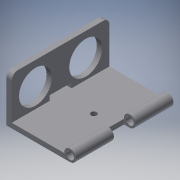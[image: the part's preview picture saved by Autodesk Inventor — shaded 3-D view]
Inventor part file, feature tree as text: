
AUTODESK INVENTOR PART (.ipt)
format: ipt  version: 2016 (Build 200138000, 138)  size: 327,168 bytes
history: native  units: in
note: dims shown in document units (in); Inventor stores cm internally (conversion verified against a paired STEP export)
features: extrude x20, sketch x20, projected_geometry x6, reference x3, fillet x2, plane x1
ambient origin geometry x8: Origin, YZ Plane, XZ Plane, XY Plane, X Axis, Y Axis, Z Axis, Center Point
bodies: Solid1 (feature_tree)
feature tree (52):
  extrude  "Extrusion1"  Depth=0.05in
  plane  "Work Plane1"
  extrude  "Extrusion2"  Depth=0.1496in
  extrude  "Extrusion3"  [1 undecoded]
  sketch  "Sketch4"  dims[d7=0.4in d8=0.0in d9=1.1in]
  extrude  "Extrusion4"  Depth=1.1in
  extrude  "Extrusion5"  Depth=1.1in
  extrude  "Extrusion6"  Depth=1.05in
  extrude  "Extrusion7"  Depth=1.05in
  extrude  "Extrusion8"  Depth=1.2in
  extrude  "Extrusion9"  Depth=1.2in
  extrude  "Extrusion10"  Depth=1.1in
  fillet  "Fillet1"  Radius=1.1in
  extrude  "Extrusion12"  Depth=1.0in TaperAngle=0.0deg
  extrude  "Extrusion13"  Depth=0.05in TaperAngle=0.0deg
  extrude  "Extrusion14"  Depth=0.8661in TaperAngle=0.0deg
  extrude  "Extrusion15"  Depth=0.3937in TaperAngle=0.0deg
  extrude  "Extrusion16"  Depth=0.125in TaperAngle=0.0deg
  extrude  "Extrusion17"  Depth=0.5906in TaperAngle=0.0deg
  extrude  "Extrusion18"  Depth=0.6693in
  extrude  "Extrusion19"  Depth=1.0in TaperAngle=0.0deg
  extrude  "Extrusion20"  Depth=0.0197in TaperAngle=0.0deg
  fillet  "Fillet2"  Radius=0.08in
  extrude  "Extrusion21"  Depth=0.44in
  sketch  "Sketch1"  dims[d0=0.15in d1=0.05in]
  sketch  "Sketch2"  dims[d2=0.2362in d3=0.1496in]
  sketch  "Sketch3"  dims[d4=1.2in d5=0.0in d6=-0.4in]
  sketch  "Sketch5"  dims[d10=1.1in d11=1.1in]
  sketch  "Sketch6"  dims[d12=0.05in d13=1.05in]
  sketch  "Sketch7"  dims[d14=0.05in d15=1.05in]
  sketch  "Sketch8"  dims[d16=1.0in d17=0.0in d18=1.2in]
  reference  "Reference1"
  sketch  "Sketch9"  dims[d19=1.2in d20=1.2in]
  projected_geometry  "Projected Loop1"
  sketch  "Sketch10"  dims[d21=1.1in d22=1.1in d23=1.1in]
  projected_geometry  "Projected Loop2"
  sketch  "Sketch12"  dims[d24=1.0in d25=0.0in d26=1.0in d27=0.0in]
  projected_geometry  "Projected Loop3"
  sketch  "Sketch13"  dims[d28=0.05in d29=0.0in d30=0.05in d31=0.0in]
  sketch  "Sketch14"  dims[d32=0.1083in d35=0.8661in d36=0.0in]
  projected_geometry  "Projected Loop4"
  sketch  "Sketch15"  dims[d37=0.3937in d38=0.0in d39=0.3937in d40=0.0in]
  sketch  "Sketch16"  dims[d45=0.125in d46=0.4724in d47=0.0in]
  reference  "Reference4"
  reference  "Reference5"
  sketch  "Sketch17"  dims[d48=199.0in d49=0.0in d50=0.5906in d51=0.0in]
  projected_geometry  "Projected Loop5"
  sketch  "Sketch18"  dims[d52=0.5906in d53=0.0in d54=0.6693in]
  projected_geometry  "Projected Loop6"
  sketch  "Sketch19"  dims[d55=0.6693in d56=1.0in d57=0.0in]
  sketch  "Sketch20"  dims[d58=0.0197in d59=0.0in d60=0.0197in d61=0.0in d62=0.08in d63=0.0in]
  sketch  "Sketch21"  dims[d64=0.22in d65=0.44in d66=0.1in d67=1.0in d68=0.0in d69=0.0098in d70=0.1969in d71=0.1969in d72=0.1181in d73=1.0in d74=0.0in]
note: 1 required parameter value undecoded (feature->parameter linkage not recoverable at this tier; creation-order binding heuristic only, values carry confidence <= 0.55)
